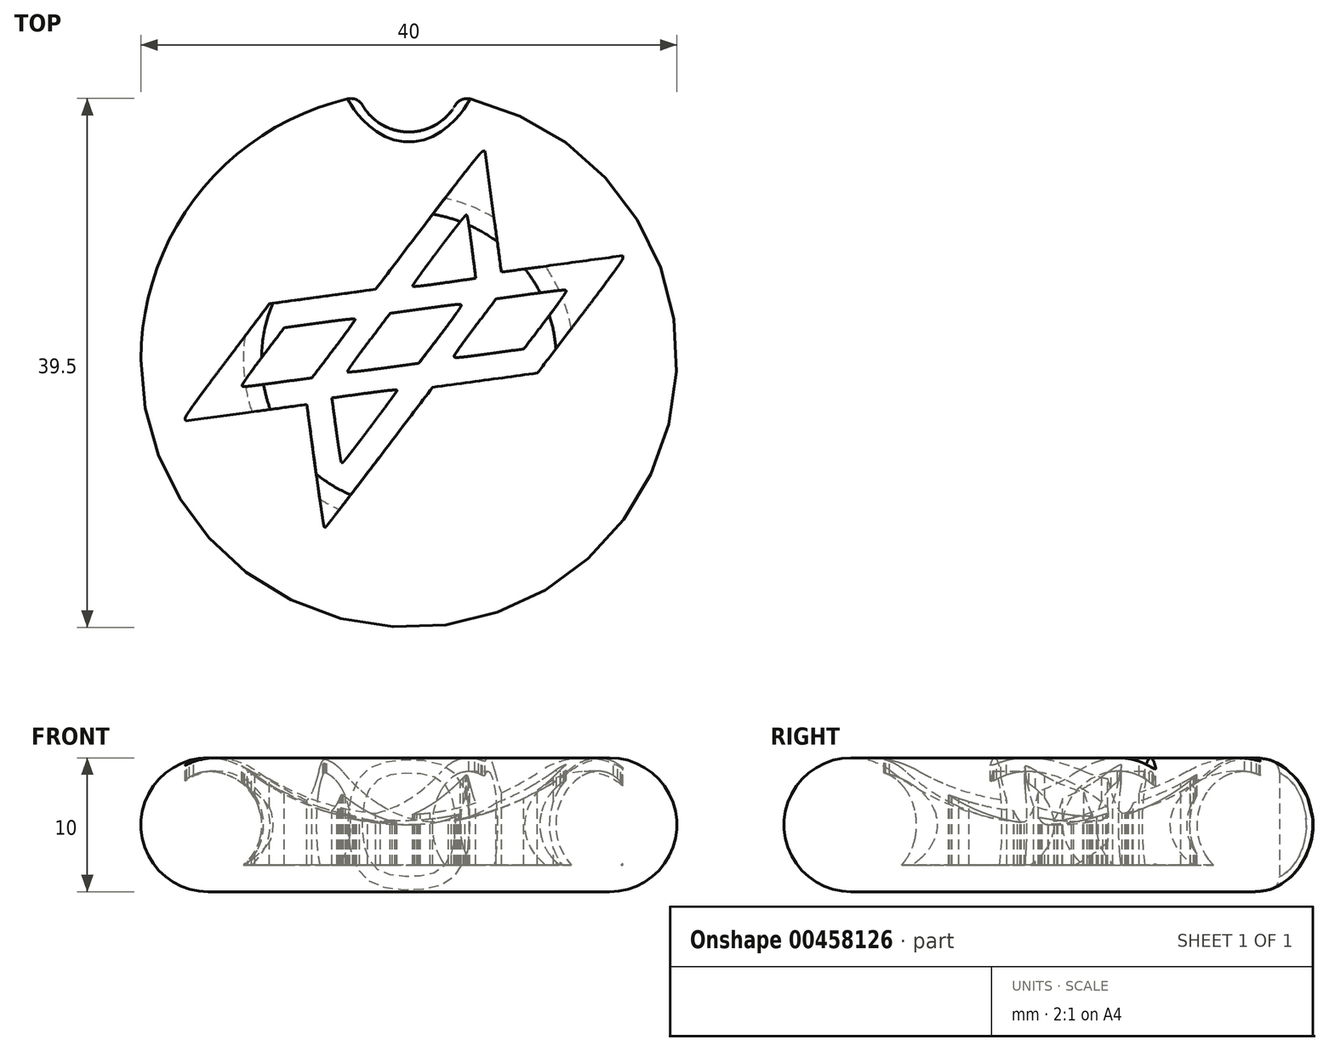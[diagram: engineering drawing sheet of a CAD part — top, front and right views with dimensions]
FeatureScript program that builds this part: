
annotation { "Feature Type Name" : "Feature", "Feature Type Description" : "" }
export const myFeature = defineFeature(function(context is Context, id is Id, definition is map)
    precondition{}
    {
        {
            var Q0;
            Q0=qCreatedBy(makeId("Front.planeOp"),FACE);
            var sketch = newSketch(context, id + "F0", { "sketchPlane" : qUnion([Q0])});
            skArc(sketch, "E0", {"start": v(-12, 9) * mm, "mid": v(-19.74, 6.58) * mm, "end": v(-15, 0) * mm});
            skArc(sketch, "E1", {"start": v(-12, 9) * mm, "mid": v(-6.32, 6.03) * mm, "end": v(0, 5) * mm});
            skLineSegment(sketch, "E2", {"start": v(0, 0) * mm, "end": v(-15, 0) * mm});
            skLineSegment(sketch, "E3", {"start": v(0, 0) * mm, "end": v(0, 5) * mm});
            skSolve(sketch);
        }
        {
            var Q0;
            Q0 = qSketchRegion(id + "F0", true);
            var Q1;
            Q1=sQuery(id+"F0.wireOp",EDGE,"E3");
            revolve(context, id + "F1", {"entities" : qUnion([Q0]), "axis" : qUnion([Q1]), "revolveType" : RevolveType.FULL});
        }
        {
            var Q0;
            Q0=qCreatedBy(makeId("Top.planeOp"),FACE);
            cPlane(context, id + "F2", {"entities" : qUnion([Q0]), "cplaneType" : CPlaneType.OFFSET, "offset" : 10 * mm, "width" : 150 * mm, "height" : 150 * mm});
        }
        {
            var Q0;
            Q0=qCreatedBy(id+"F2.planeOp",FACE);
            var sketch = newSketch(context, id + "F3", { "sketchPlane" : qUnion([Q0])});
            skLineSegment(sketch, "E4", {"start": v(-6.32, -12.5) * mm, "end": v(-6.35, -12.4) * mm});
            skLineSegment(sketch, "E5", {"start": v(-6.35, -12.4) * mm, "end": v(-6.4, -12.12) * mm});
            skLineSegment(sketch, "E6", {"start": v(-6.4, -12.12) * mm, "end": v(-6.46, -11.7) * mm});
            skLineSegment(sketch, "E7", {"start": v(-6.46, -11.7) * mm, "end": v(-6.55, -11.13) * mm});
            skLineSegment(sketch, "E8", {"start": v(-6.55, -11.13) * mm, "end": v(-6.65, -10.45) * mm});
            skLineSegment(sketch, "E9", {"start": v(-6.65, -10.45) * mm, "end": v(-6.76, -9.67) * mm});
            skLineSegment(sketch, "E10", {"start": v(-6.76, -9.67) * mm, "end": v(-6.88, -8.82) * mm});
            skLineSegment(sketch, "E11", {"start": v(-6.88, -8.82) * mm, "end": v(-7, -7.9) * mm});
            skLineSegment(sketch, "E12", {"start": v(-7, -7.9) * mm, "end": v(-7.62, -3.35) * mm});
            skLineSegment(sketch, "E13", {"start": v(-7.62, -3.35) * mm, "end": v(-12.15, -3.97) * mm});
            skLineSegment(sketch, "E14", {"start": v(-12.15, -3.97) * mm, "end": v(-16.67, -4.59) * mm});
            skLineSegment(sketch, "E15", {"start": v(-16.67, -4.59) * mm, "end": v(-16.7, -4.4) * mm});
            skLineSegment(sketch, "E16", {"start": v(-16.7, -4.4) * mm, "end": v(-16.67, -4.3) * mm});
            skLineSegment(sketch, "E17", {"start": v(-16.67, -4.3) * mm, "end": v(-16.57, -4.11) * mm});
            skLineSegment(sketch, "E18", {"start": v(-16.57, -4.11) * mm, "end": v(-16.37, -3.81) * mm});
            skLineSegment(sketch, "E19", {"start": v(-16.37, -3.81) * mm, "end": v(-16.07, -3.39) * mm});
            skLineSegment(sketch, "E20", {"start": v(-16.07, -3.39) * mm, "end": v(-15.66, -2.81) * mm});
            skLineSegment(sketch, "E21", {"start": v(-15.66, -2.81) * mm, "end": v(-15.1, -2.07) * mm});
            skLineSegment(sketch, "E22", {"start": v(-15.1, -2.07) * mm, "end": v(-14.42, -1.15) * mm});
            skLineSegment(sketch, "E23", {"start": v(-14.42, -1.15) * mm, "end": v(-13.57, -0.02) * mm});
            skLineSegment(sketch, "E24", {"start": v(-13.57, -0.02) * mm, "end": v(-10.4, 4.17) * mm});
            skLineSegment(sketch, "E25", {"start": v(-10.4, 4.17) * mm, "end": v(-6.44, 4.7) * mm});
            skLineSegment(sketch, "E26", {"start": v(-6.44, 4.7) * mm, "end": v(-2.48, 5.25) * mm});
            skLineSegment(sketch, "E27", {"start": v(-2.48, 5.25) * mm, "end": v(1.43, 10.4) * mm});
            skLineSegment(sketch, "E28", {"start": v(1.43, 10.4) * mm, "end": v(2.42, 11.7) * mm});
            skLineSegment(sketch, "E29", {"start": v(2.42, 11.7) * mm, "end": v(3.25, 12.78) * mm});
            skLineSegment(sketch, "E30", {"start": v(3.25, 12.78) * mm, "end": v(3.94, 13.67) * mm});
            skLineSegment(sketch, "E31", {"start": v(3.94, 13.67) * mm, "end": v(4.49, 14.37) * mm});
            skLineSegment(sketch, "E32", {"start": v(4.49, 14.37) * mm, "end": v(4.91, 14.9) * mm});
            skLineSegment(sketch, "E33", {"start": v(4.91, 14.9) * mm, "end": v(5.22, 15.27) * mm});
            skLineSegment(sketch, "E34", {"start": v(5.22, 15.27) * mm, "end": v(5.41, 15.48) * mm});
            skLineSegment(sketch, "E35", {"start": v(5.41, 15.48) * mm, "end": v(5.5, 15.56) * mm});
            skLineSegment(sketch, "E36", {"start": v(5.5, 15.56) * mm, "end": v(5.68, 15.58) * mm});
            skLineSegment(sketch, "E37", {"start": v(5.68, 15.58) * mm, "end": v(6.3, 11.05) * mm});
            skLineSegment(sketch, "E38", {"start": v(6.3, 11.05) * mm, "end": v(6.91, 6.53) * mm});
            skLineSegment(sketch, "E39", {"start": v(6.91, 6.53) * mm, "end": v(11.44, 7.15) * mm});
            skLineSegment(sketch, "E40", {"start": v(11.44, 7.15) * mm, "end": v(15.96, 7.76) * mm});
            skLineSegment(sketch, "E41", {"start": v(15.96, 7.76) * mm, "end": v(15.98, 7.6) * mm});
            skLineSegment(sketch, "E42", {"start": v(15.98, 7.6) * mm, "end": v(15.95, 7.5) * mm});
            skLineSegment(sketch, "E43", {"start": v(15.95, 7.5) * mm, "end": v(15.82, 7.29) * mm});
            skLineSegment(sketch, "E44", {"start": v(15.82, 7.29) * mm, "end": v(15.6, 6.96) * mm});
            skLineSegment(sketch, "E45", {"start": v(15.6, 6.96) * mm, "end": v(15.28, 6.5) * mm});
            skLineSegment(sketch, "E46", {"start": v(15.28, 6.5) * mm, "end": v(14.84, 5.91) * mm});
            skLineSegment(sketch, "E47", {"start": v(14.84, 5.91) * mm, "end": v(14.29, 5.17) * mm});
            skLineSegment(sketch, "E48", {"start": v(14.29, 5.17) * mm, "end": v(13.61, 4.27) * mm});
            skLineSegment(sketch, "E49", {"start": v(13.61, 4.27) * mm, "end": v(12.8, 3.2) * mm});
            skLineSegment(sketch, "E50", {"start": v(12.8, 3.2) * mm, "end": v(9.6, -1) * mm});
            skLineSegment(sketch, "E51", {"start": v(9.6, -1) * mm, "end": v(5.68, -1.54) * mm});
            skLineSegment(sketch, "E52", {"start": v(5.68, -1.54) * mm, "end": v(1.77, -2.07) * mm});
            skLineSegment(sketch, "E53", {"start": v(1.77, -2.07) * mm, "end": v(-2.2, -7.3) * mm});
            skLineSegment(sketch, "E54", {"start": v(-2.2, -7.3) * mm, "end": v(-3, -8.35) * mm});
            skLineSegment(sketch, "E55", {"start": v(-3, -8.35) * mm, "end": v(-3.75, -9.33) * mm});
            skLineSegment(sketch, "E56", {"start": v(-3.75, -9.33) * mm, "end": v(-4.43, -10.22) * mm});
            skLineSegment(sketch, "E57", {"start": v(-4.43, -10.22) * mm, "end": v(-5.02, -11) * mm});
            skLineSegment(sketch, "E58", {"start": v(-5.02, -11) * mm, "end": v(-5.52, -11.64) * mm});
            skLineSegment(sketch, "E59", {"start": v(-5.52, -11.64) * mm, "end": v(-5.9, -12.12) * mm});
            skLineSegment(sketch, "E60", {"start": v(-5.9, -12.12) * mm, "end": v(-6.13, -12.43) * mm});
            skLineSegment(sketch, "E61", {"start": v(-6.13, -12.43) * mm, "end": v(-6.22, -12.53) * mm});
            skLineSegment(sketch, "E62", {"start": v(-6.22, -12.53) * mm, "end": v(-6.32, -12.5) * mm});
            skLineSegment(sketch, "E63", {"start": v(-5.04, -7.67) * mm, "end": v(-5.1, -7.47) * mm});
            skLineSegment(sketch, "E64", {"start": v(-5.1, -7.47) * mm, "end": v(-5.18, -6.94) * mm});
            skLineSegment(sketch, "E65", {"start": v(-5.18, -6.94) * mm, "end": v(-5.3, -6.18) * mm});
            skLineSegment(sketch, "E66", {"start": v(-5.3, -6.18) * mm, "end": v(-5.43, -5.25) * mm});
            skLineSegment(sketch, "E67", {"start": v(-5.43, -5.25) * mm, "end": v(-5.75, -2.87) * mm});
            skLineSegment(sketch, "E68", {"start": v(-5.75, -2.87) * mm, "end": v(-3.32, -2.53) * mm});
            skLineSegment(sketch, "E69", {"start": v(-3.32, -2.53) * mm, "end": v(-2.14, -2.38) * mm});
            skLineSegment(sketch, "E70", {"start": v(-2.14, -2.38) * mm, "end": v(-1.39, -2.3) * mm});
            skLineSegment(sketch, "E71", {"start": v(-1.39, -2.3) * mm, "end": v(-1, -2.27) * mm});
            skLineSegment(sketch, "E72", {"start": v(-1, -2.27) * mm, "end": v(-0.87, -2.3) * mm});
            skLineSegment(sketch, "E73", {"start": v(-0.87, -2.3) * mm, "end": v(-0.92, -2.37) * mm});
            skLineSegment(sketch, "E74", {"start": v(-0.92, -2.37) * mm, "end": v(-1.04, -2.56) * mm});
            skLineSegment(sketch, "E75", {"start": v(-1.04, -2.56) * mm, "end": v(-1.24, -2.83) * mm});
            skLineSegment(sketch, "E76", {"start": v(-1.24, -2.83) * mm, "end": v(-1.5, -3.18) * mm});
            skLineSegment(sketch, "E77", {"start": v(-1.5, -3.18) * mm, "end": v(-1.8, -3.6) * mm});
            skLineSegment(sketch, "E78", {"start": v(-1.8, -3.6) * mm, "end": v(-2.13, -4.05) * mm});
            skLineSegment(sketch, "E79", {"start": v(-2.13, -4.05) * mm, "end": v(-2.5, -4.53) * mm});
            skLineSegment(sketch, "E80", {"start": v(-2.5, -4.53) * mm, "end": v(-2.87, -5.03) * mm});
            skLineSegment(sketch, "E81", {"start": v(-2.87, -5.03) * mm, "end": v(-3.25, -5.53) * mm});
            skLineSegment(sketch, "E82", {"start": v(-3.25, -5.53) * mm, "end": v(-3.61, -6.02) * mm});
            skLineSegment(sketch, "E83", {"start": v(-3.61, -6.02) * mm, "end": v(-3.96, -6.47) * mm});
            skLineSegment(sketch, "E84", {"start": v(-3.96, -6.47) * mm, "end": v(-4.27, -6.87) * mm});
            skLineSegment(sketch, "E85", {"start": v(-4.27, -6.87) * mm, "end": v(-4.53, -7.22) * mm});
            skLineSegment(sketch, "E86", {"start": v(-4.53, -7.22) * mm, "end": v(-4.74, -7.48) * mm});
            skLineSegment(sketch, "E87", {"start": v(-4.74, -7.48) * mm, "end": v(-4.88, -7.65) * mm});
            skLineSegment(sketch, "E88", {"start": v(-4.88, -7.65) * mm, "end": v(-4.94, -7.71) * mm});
            skLineSegment(sketch, "E89", {"start": v(-4.94, -7.71) * mm, "end": v(-5.04, -7.67) * mm});
            skLineSegment(sketch, "E90", {"start": v(-12.46, -1.94) * mm, "end": v(-12.34, -1.72) * mm});
            skLineSegment(sketch, "E91", {"start": v(-12.34, -1.72) * mm, "end": v(-12, -1.23) * mm});
            skLineSegment(sketch, "E92", {"start": v(-12, -1.23) * mm, "end": v(-11.5, -0.54) * mm});
            skLineSegment(sketch, "E93", {"start": v(-11.5, -0.54) * mm, "end": v(-10.89, 0.29) * mm});
            skLineSegment(sketch, "E94", {"start": v(-10.89, 0.29) * mm, "end": v(-9.3, 2.38) * mm});
            skLineSegment(sketch, "E95", {"start": v(-9.3, 2.38) * mm, "end": v(-6.65, 2.74) * mm});
            skLineSegment(sketch, "E96", {"start": v(-6.65, 2.74) * mm, "end": v(-5.36, 2.92) * mm});
            skLineSegment(sketch, "E97", {"start": v(-5.36, 2.92) * mm, "end": v(-4.55, 3.01) * mm});
            skLineSegment(sketch, "E98", {"start": v(-4.55, 3.01) * mm, "end": v(-4.12, 3.04) * mm});
            skLineSegment(sketch, "E99", {"start": v(-4.12, 3.04) * mm, "end": v(-4, 3) * mm});
            skLineSegment(sketch, "E100", {"start": v(-4, 3) * mm, "end": v(-4.12, 2.8) * mm});
            skLineSegment(sketch, "E101", {"start": v(-4.12, 2.8) * mm, "end": v(-4.47, 2.31) * mm});
            skLineSegment(sketch, "E102", {"start": v(-4.47, 2.31) * mm, "end": v(-4.98, 1.61) * mm});
            skLineSegment(sketch, "E103", {"start": v(-4.98, 1.61) * mm, "end": v(-5.6, 0.77) * mm});
            skLineSegment(sketch, "E104", {"start": v(-5.6, 0.77) * mm, "end": v(-7.24, -1.36) * mm});
            skLineSegment(sketch, "E105", {"start": v(-7.24, -1.36) * mm, "end": v(-9.84, -1.72) * mm});
            skLineSegment(sketch, "E106", {"start": v(-9.84, -1.72) * mm, "end": v(-10.65, -1.83) * mm});
            skLineSegment(sketch, "E107", {"start": v(-10.65, -1.83) * mm, "end": v(-11.27, -1.91) * mm});
            skLineSegment(sketch, "E108", {"start": v(-11.27, -1.91) * mm, "end": v(-11.74, -1.97) * mm});
            skLineSegment(sketch, "E109", {"start": v(-11.74, -1.97) * mm, "end": v(-12.06, -2) * mm});
            skLineSegment(sketch, "E110", {"start": v(-12.06, -2) * mm, "end": v(-12.27, -2.01) * mm});
            skLineSegment(sketch, "E111", {"start": v(-12.27, -2.01) * mm, "end": v(-12.39, -2) * mm});
            skLineSegment(sketch, "E112", {"start": v(-12.39, -2) * mm, "end": v(-12.44, -1.98) * mm});
            skLineSegment(sketch, "E113", {"start": v(-12.44, -1.98) * mm, "end": v(-12.46, -1.94) * mm});
            skLineSegment(sketch, "E114", {"start": v(-4.59, -0.92) * mm, "end": v(-4.5, -0.73) * mm});
            skLineSegment(sketch, "E115", {"start": v(-4.5, -0.73) * mm, "end": v(-4.18, -0.26) * mm});
            skLineSegment(sketch, "E116", {"start": v(-4.18, -0.26) * mm, "end": v(-3.68, 0.44) * mm});
            skLineSegment(sketch, "E117", {"start": v(-3.68, 0.44) * mm, "end": v(-3.02, 1.31) * mm});
            skLineSegment(sketch, "E118", {"start": v(-3.02, 1.31) * mm, "end": v(-1.39, 3.46) * mm});
            skLineSegment(sketch, "E119", {"start": v(-1.39, 3.46) * mm, "end": v(1.26, 3.82) * mm});
            skLineSegment(sketch, "E120", {"start": v(1.26, 3.82) * mm, "end": v(2.08, 3.93) * mm});
            skLineSegment(sketch, "E121", {"start": v(2.08, 3.93) * mm, "end": v(2.72, 4.02) * mm});
            skLineSegment(sketch, "E122", {"start": v(2.72, 4.02) * mm, "end": v(3.18, 4.08) * mm});
            skLineSegment(sketch, "E123", {"start": v(3.18, 4.08) * mm, "end": v(3.51, 4.1) * mm});
            skLineSegment(sketch, "E124", {"start": v(3.51, 4.1) * mm, "end": v(3.72, 4.12) * mm});
            skLineSegment(sketch, "E125", {"start": v(3.72, 4.12) * mm, "end": v(3.84, 4.11) * mm});
            skLineSegment(sketch, "E126", {"start": v(3.84, 4.11) * mm, "end": v(3.9, 4.09) * mm});
            skLineSegment(sketch, "E127", {"start": v(3.9, 4.09) * mm, "end": v(3.92, 4.05) * mm});
            skLineSegment(sketch, "E128", {"start": v(3.92, 4.05) * mm, "end": v(3.8, 3.83) * mm});
            skLineSegment(sketch, "E129", {"start": v(3.8, 3.83) * mm, "end": v(3.47, 3.34) * mm});
            skLineSegment(sketch, "E130", {"start": v(3.47, 3.34) * mm, "end": v(2.96, 2.65) * mm});
            skLineSegment(sketch, "E131", {"start": v(2.96, 2.65) * mm, "end": v(2.34, 1.82) * mm});
            skLineSegment(sketch, "E132", {"start": v(2.34, 1.82) * mm, "end": v(0.74, -0.28) * mm});
            skLineSegment(sketch, "E133", {"start": v(0.74, -0.28) * mm, "end": v(-1.9, -0.64) * mm});
            skLineSegment(sketch, "E134", {"start": v(-1.9, -0.64) * mm, "end": v(-3.09, -0.8) * mm});
            skLineSegment(sketch, "E135", {"start": v(-3.09, -0.8) * mm, "end": v(-3.92, -0.9) * mm});
            skLineSegment(sketch, "E136", {"start": v(-3.92, -0.9) * mm, "end": v(-4.41, -0.93) * mm});
            skLineSegment(sketch, "E137", {"start": v(-4.41, -0.93) * mm, "end": v(-4.59, -0.92) * mm});
            skLineSegment(sketch, "E138", {"start": v(3.38, 0.2) * mm, "end": v(3.44, 0.38) * mm});
            skLineSegment(sketch, "E139", {"start": v(3.44, 0.38) * mm, "end": v(3.7, 0.78) * mm});
            skLineSegment(sketch, "E140", {"start": v(3.7, 0.78) * mm, "end": v(4.19, 1.46) * mm});
            skLineSegment(sketch, "E141", {"start": v(4.19, 1.46) * mm, "end": v(4.92, 2.43) * mm});
            skLineSegment(sketch, "E142", {"start": v(4.92, 2.43) * mm, "end": v(6.52, 4.54) * mm});
            skLineSegment(sketch, "E143", {"start": v(6.52, 4.54) * mm, "end": v(9.13, 4.9) * mm});
            skLineSegment(sketch, "E144", {"start": v(9.13, 4.9) * mm, "end": v(9.94, 5) * mm});
            skLineSegment(sketch, "E145", {"start": v(9.94, 5) * mm, "end": v(10.57, 5.09) * mm});
            skLineSegment(sketch, "E146", {"start": v(10.57, 5.09) * mm, "end": v(11.03, 5.14) * mm});
            skLineSegment(sketch, "E147", {"start": v(11.03, 5.14) * mm, "end": v(11.35, 5.18) * mm});
            skLineSegment(sketch, "E148", {"start": v(11.35, 5.18) * mm, "end": v(11.56, 5.19) * mm});
            skLineSegment(sketch, "E149", {"start": v(11.56, 5.19) * mm, "end": v(11.68, 5.18) * mm});
            skLineSegment(sketch, "E150", {"start": v(11.68, 5.18) * mm, "end": v(11.73, 5.16) * mm});
            skLineSegment(sketch, "E151", {"start": v(11.73, 5.16) * mm, "end": v(11.75, 5.11) * mm});
            skLineSegment(sketch, "E152", {"start": v(11.75, 5.11) * mm, "end": v(11.63, 4.9) * mm});
            skLineSegment(sketch, "E153", {"start": v(11.63, 4.9) * mm, "end": v(11.3, 4.4) * mm});
            skLineSegment(sketch, "E154", {"start": v(11.3, 4.4) * mm, "end": v(10.8, 3.72) * mm});
            skLineSegment(sketch, "E155", {"start": v(10.8, 3.72) * mm, "end": v(10.17, 2.89) * mm});
            skLineSegment(sketch, "E156", {"start": v(10.17, 2.89) * mm, "end": v(8.58, 0.8) * mm});
            skLineSegment(sketch, "E157", {"start": v(8.58, 0.8) * mm, "end": v(6.01, 0.44) * mm});
            skLineSegment(sketch, "E158", {"start": v(6.01, 0.44) * mm, "end": v(5.24, 0.34) * mm});
            skLineSegment(sketch, "E159", {"start": v(5.24, 0.34) * mm, "end": v(4.65, 0.26) * mm});
            skLineSegment(sketch, "E160", {"start": v(4.65, 0.26) * mm, "end": v(4.2, 0.2) * mm});
            skLineSegment(sketch, "E161", {"start": v(4.2, 0.2) * mm, "end": v(3.86, 0.17) * mm});
            skLineSegment(sketch, "E162", {"start": v(3.86, 0.17) * mm, "end": v(3.64, 0.16) * mm});
            skLineSegment(sketch, "E163", {"start": v(3.64, 0.16) * mm, "end": v(3.5, 0.16) * mm});
            skLineSegment(sketch, "E164", {"start": v(3.5, 0.16) * mm, "end": v(3.42, 0.18) * mm});
            skLineSegment(sketch, "E165", {"start": v(3.42, 0.18) * mm, "end": v(3.38, 0.2) * mm});
            skLineSegment(sketch, "E166", {"start": v(0.27, 5.48) * mm, "end": v(0.3, 5.55) * mm});
            skLineSegment(sketch, "E167", {"start": v(0.3, 5.55) * mm, "end": v(0.42, 5.73) * mm});
            skLineSegment(sketch, "E168", {"start": v(0.42, 5.73) * mm, "end": v(0.6, 6) * mm});
            skLineSegment(sketch, "E169", {"start": v(0.6, 6) * mm, "end": v(0.85, 6.35) * mm});
            skLineSegment(sketch, "E170", {"start": v(0.85, 6.35) * mm, "end": v(1.14, 6.75) * mm});
            skLineSegment(sketch, "E171", {"start": v(1.14, 6.75) * mm, "end": v(1.47, 7.2) * mm});
            skLineSegment(sketch, "E172", {"start": v(1.47, 7.2) * mm, "end": v(1.83, 7.68) * mm});
            skLineSegment(sketch, "E173", {"start": v(1.83, 7.68) * mm, "end": v(2.2, 8.17) * mm});
            skLineSegment(sketch, "E174", {"start": v(2.2, 8.17) * mm, "end": v(2.57, 8.67) * mm});
            skLineSegment(sketch, "E175", {"start": v(2.57, 8.67) * mm, "end": v(2.93, 9.14) * mm});
            skLineSegment(sketch, "E176", {"start": v(2.93, 9.14) * mm, "end": v(3.28, 9.59) * mm});
            skLineSegment(sketch, "E177", {"start": v(3.28, 9.59) * mm, "end": v(3.59, 9.99) * mm});
            skLineSegment(sketch, "E178", {"start": v(3.59, 9.99) * mm, "end": v(3.86, 10.33) * mm});
            skLineSegment(sketch, "E179", {"start": v(3.86, 10.33) * mm, "end": v(4.07, 10.59) * mm});
            skLineSegment(sketch, "E180", {"start": v(4.07, 10.59) * mm, "end": v(4.22, 10.76) * mm});
            skLineSegment(sketch, "E181", {"start": v(4.22, 10.76) * mm, "end": v(4.3, 10.82) * mm});
            skLineSegment(sketch, "E182", {"start": v(4.3, 10.82) * mm, "end": v(4.35, 10.72) * mm});
            skLineSegment(sketch, "E183", {"start": v(4.35, 10.72) * mm, "end": v(4.43, 10.35) * mm});
            skLineSegment(sketch, "E184", {"start": v(4.43, 10.35) * mm, "end": v(4.54, 9.62) * mm});
            skLineSegment(sketch, "E185", {"start": v(4.54, 9.62) * mm, "end": v(4.7, 8.45) * mm});
            skLineSegment(sketch, "E186", {"start": v(4.7, 8.45) * mm, "end": v(5, 6.07) * mm});
            skLineSegment(sketch, "E187", {"start": v(5, 6.07) * mm, "end": v(2.67, 5.74) * mm});
            skLineSegment(sketch, "E188", {"start": v(2.67, 5.74) * mm, "end": v(1.6, 5.59) * mm});
            skLineSegment(sketch, "E189", {"start": v(1.6, 5.59) * mm, "end": v(0.86, 5.5) * mm});
            skLineSegment(sketch, "E190", {"start": v(0.86, 5.5) * mm, "end": v(0.43, 5.46) * mm});
            skLineSegment(sketch, "E191", {"start": v(0.43, 5.46) * mm, "end": v(0.27, 5.48) * mm});
            skSolve(sketch);
        }
        {
            var Q0;
            Q0 = qSketchRegion(id + "F3", true);
            extrude(context, id + "F4", {"entities" : qUnion([Q0]), "operationType" : NewBodyOperationType.REMOVE, "oppositeDirection" : true, "depth" : 8 * mm});
        }
        {
            var Q0;
            Q0=qCreatedBy(makeId("Front.planeOp"),FACE);
            var sketch = newSketch(context, id + "F5", { "sketchPlane" : qUnion([Q0])});
            skCircle(sketch, "E192", {"center": v(-15, 5) * mm, "radius": 4 * mm});
            skSolve(sketch);
        }
        {
            var Q0;
            Q0 = qSketchRegion(id + "F5", true);
            var Q1;
            Q1=sQuery(id+"F0.wireOp",EDGE,"E3");
            revolve(context, id + "F6", {"operationType" : NewBodyOperationType.ADD, "entities" : qUnion([Q0]), "axis" : qUnion([Q1]), "revolveType" : RevolveType.FULL});
        }
        {
            var Q0;
            Q0=qCreatedBy(makeId("Top.planeOp"),FACE);
            var sketch = newSketch(context, id + "F7", { "sketchPlane" : qUnion([Q0])});
            skCircle(sketch, "E193", {"center": v(0, 21) * mm, "radius": 4 * mm});
            skSolve(sketch);
        }
        {
            var Q0;
            Q0 = qSketchRegion(id + "F7", true);
            extrude(context, id + "F8", {"entities" : qUnion([Q0]), "operationType" : NewBodyOperationType.REMOVE, "depth" : 25 * mm});
        }
        {
            var Q0;
            Q0=makeQuery(id+"F8.boolean.opBoolean","INTERSECT",EDGE,{"derivedFrom":[makeQuery(id+"F4.boolean.opBoolean","SPLIT",FACE,{"disambiguationData":[TD([makeQuery(id+"F1.opRevolve","SWEPT_FACE",FACE,{"disambiguationData":[OSD([sQuery(id+"F0.wireOp",EDGE,"E2")])]})])],"derivedFrom":makeQuery(id+"F1.opRevolve","SWEPT_FACE",FACE,{"disambiguationData":[OSD([sQuery(id+"F0.wireOp",EDGE,"E0")])]})}),makeQuery(id+"F8.opExtrude","SWEPT_FACE",FACE,{"disambiguationData":[OSD([sQuery(id+"F7.wireOp",EDGE,"E193")])]})]});
            fillet(context, id + "F9", {"entities" : qUnion([Q0]), "radius" : 1 * mm, "tangentPropagation" : true, "allowEdgeOverflow" : false});
        }
    });
